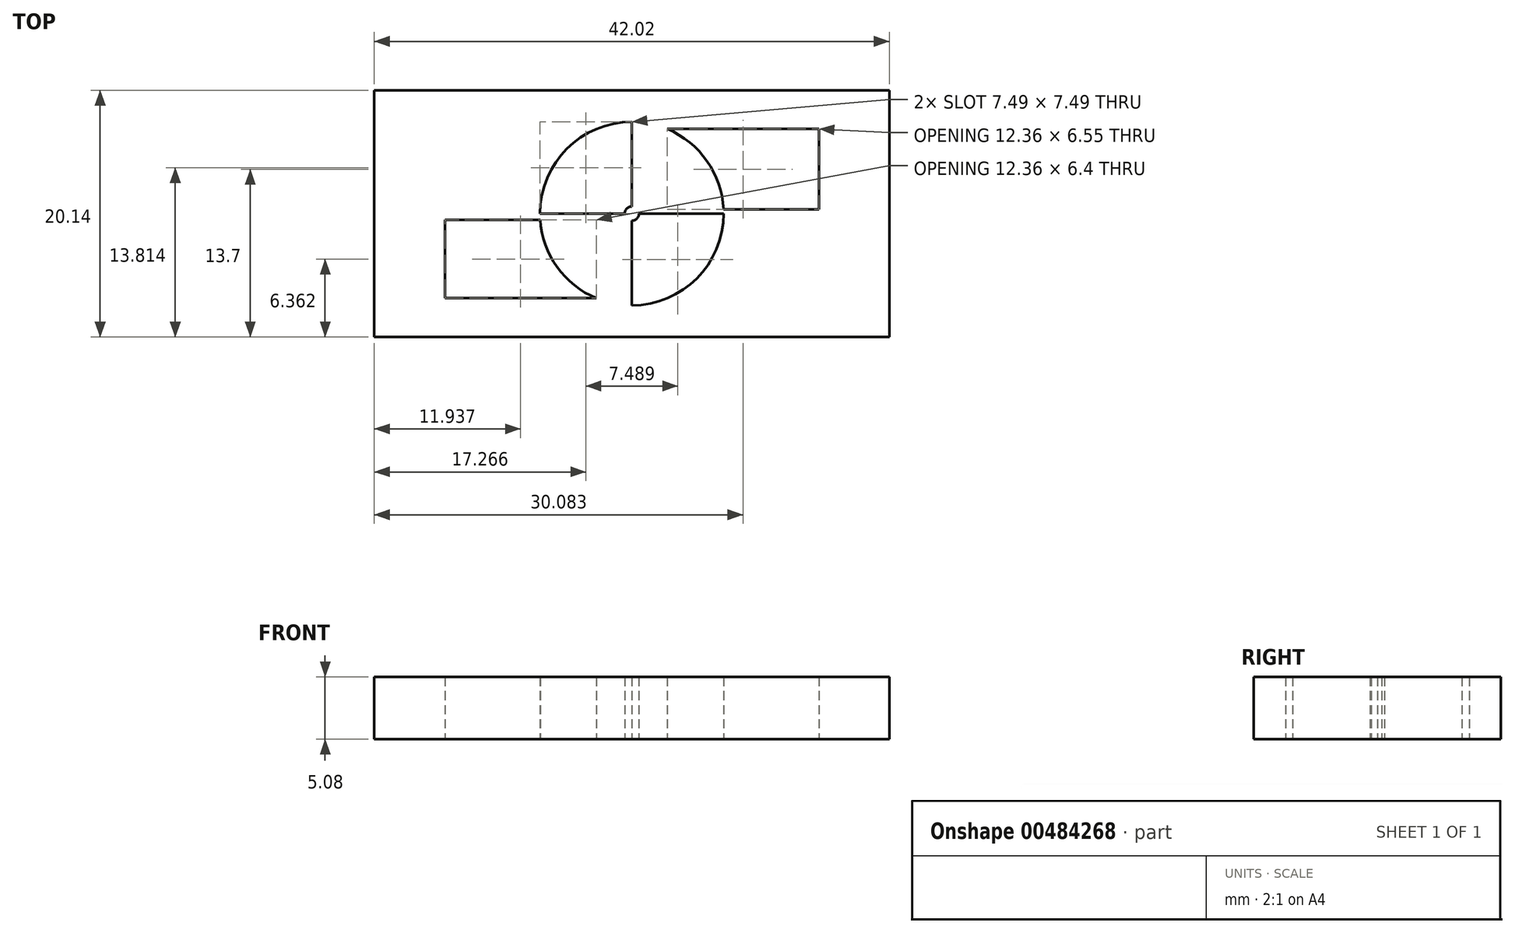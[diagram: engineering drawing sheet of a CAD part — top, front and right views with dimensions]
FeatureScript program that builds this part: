
annotation { "Feature Type Name" : "Feature", "Feature Type Description" : "" }
export const myFeature = defineFeature(function(context is Context, id is Id, definition is map)
    precondition{}
    {
        {
            var Q0;
            Q0=qCreatedBy(makeId("Top.planeOp"),FACE);
            var sketch = newSketch(context, id + "F0", { "sketchPlane" : qUnion([Q0])});
            skLineSegment(sketch, "E0.top", {"start": v(0, 10.07) * mm, "end": v(-21, 10.07) * mm});
            skLineSegment(sketch, "E0.right", {"start": v(-21, 0) * mm, "end": v(-21, 10.07) * mm});
            skLineSegment(sketch, "E1.MirrorCS", {"start": v(-21, 0) * mm, "end": v(-21, -10.07) * mm});
            skLineSegment(sketch, "E2.MirrorCS", {"start": v(0, -10.07) * mm, "end": v(-21, -10.07) * mm});
            skLineSegment(sketch, "E3.MirrorCS", {"start": v(0, 10.07) * mm, "end": v(21, 10.07) * mm});
            skLineSegment(sketch, "E4.MirrorCS", {"start": v(21, 0) * mm, "end": v(21, 10.07) * mm});
            skLineSegment(sketch, "E5.MirrorCS", {"start": v(0, -10.07) * mm, "end": v(21, -10.07) * mm});
            skLineSegment(sketch, "E6.MirrorCS", {"start": v(21, 0) * mm, "end": v(21, -10.07) * mm});
            skCircle(sketch, "E7", {"center": v(0, 0) * mm, "radius": 7.49 * mm});
            skLineSegment(sketch, "E8.right", {"start": v(-15.25, 0) * mm, "end": v(-15.25, -6.9) * mm});
            skLineSegment(sketch, "E9.MirrorCS", {"start": v(-15.25, 0) * mm, "end": v(-15.25, 6.9) * mm});
            skLineSegment(sketch, "E10.MirrorCS", {"start": v(15.25, 0) * mm, "end": v(15.25, 6.9) * mm});
            skLineSegment(sketch, "E11.MirrorCS", {"start": v(15.25, 0) * mm, "end": v(15.25, -6.9) * mm});
            skPoint(sketch, "E12", {"position": v(-2.9, 6.9) * mm});
            skPoint(sketch, "E13", {"position": v(-15.25, 6.9) * mm});
            skLineSegment(sketch, "E14", {"start": v(-15.25, 6.9) * mm, "end": v(-2.9, 6.9) * mm});
            skPoint(sketch, "E15", {"position": v(-2.9, -6.9) * mm});
            skPoint(sketch, "E16", {"position": v(2.9, -6.9) * mm});
            skPoint(sketch, "E17", {"position": v(2.9, 6.9) * mm});
            skLineSegment(sketch, "E18", {"start": v(2.9, 6.9) * mm, "end": v(15.25, 6.9) * mm});
            skLineSegment(sketch, "E19", {"start": v(2.9, -6.9) * mm, "end": v(15.25, -6.9) * mm});
            skLineSegment(sketch, "E20", {"start": v(-2.9, -6.9) * mm, "end": v(-15.25, -6.9) * mm});
            skLineSegment(sketch, "E21", {"start": v(0, 0) * mm, "end": v(0, 7.49) * mm});
            skLineSegment(sketch, "E22", {"start": v(0, 0) * mm, "end": v(0, -7.49) * mm});
            skLineSegment(sketch, "E23", {"start": v(-7.49, 0) * mm, "end": v(0, 0) * mm});
            skLineSegment(sketch, "E24", {"start": v(0, 0) * mm, "end": v(7.49, 0) * mm});
            skLineSegment(sketch, "E25", {"start": v(7.49, 0) * mm, "end": v(-7.49, 0) * mm});
            skPoint(sketch, "E26", {"position": v(-7.47, -0.5) * mm});
            skPoint(sketch, "E27", {"position": v(7.48, 0.35) * mm});
            skLineSegment(sketch, "E28", {"start": v(7.48, 0.35) * mm, "end": v(15.25, 0.35) * mm});
            skLineSegment(sketch, "E29", {"start": v(-7.47, -0.5) * mm, "end": v(-15.25, -0.5) * mm});
            skCircle(sketch, "E30", {"center": v(0, 0) * mm, "radius": 0.58 * mm});
            skSolve(sketch);
        }
        {
            var Q0;
            {var subQ1=sQuery(id+"F0.wireOp",EDGE,"E21");var subQ3=sQuery(id+"F0.wireOp",EDGE,"E30");var subQ4=makeQuery(id+"F0.imprint","INTERSECT",VERTEX,{"derivedFrom":[subQ1,subQ3]});Q0=makeQuery(id+"F0.imprint","IMPRINT",FACE,{"disambiguationData":[TD([[makeQuery(id+"F0.imprint","IMPRINT",EDGE,{"disambiguationData":[TD([[subQ4,-1.0]])],"derivedFrom":subQ3}),1.0]])]});}
            var Q1;
            {var subQ1=sQuery(id+"F0.wireOp",EDGE,"E21");var subQ3=sQuery(id+"F0.wireOp",EDGE,"E30");var subQ4=makeQuery(id+"F0.imprint","INTERSECT",VERTEX,{"derivedFrom":[subQ1,subQ3]});Q1=makeQuery(id+"F0.imprint","IMPRINT",FACE,{"disambiguationData":[TD([[makeQuery(id+"F0.imprint","IMPRINT",EDGE,{"disambiguationData":[TD([[subQ4,1.0]])],"derivedFrom":subQ3}),1.0]])]});}
            var Q2;
            {var subQ1=sQuery(id+"F0.wireOp",EDGE,"E22");var subQ3=sQuery(id+"F0.wireOp",EDGE,"E30");var subQ4=makeQuery(id+"F0.imprint","INTERSECT",VERTEX,{"derivedFrom":[subQ1,subQ3]});Q2=makeQuery(id+"F0.imprint","IMPRINT",FACE,{"disambiguationData":[TD([[makeQuery(id+"F0.imprint","IMPRINT",EDGE,{"disambiguationData":[TD([[subQ4,-1.0]])],"derivedFrom":subQ3}),1.0]])]});}
            var Q3;
            {var subQ1=sQuery(id+"F0.wireOp",EDGE,"E22");var subQ3=sQuery(id+"F0.wireOp",EDGE,"E30");var subQ4=makeQuery(id+"F0.imprint","INTERSECT",VERTEX,{"derivedFrom":[subQ1,subQ3]});Q3=makeQuery(id+"F0.imprint","IMPRINT",FACE,{"disambiguationData":[TD([[makeQuery(id+"F0.imprint","IMPRINT",EDGE,{"disambiguationData":[TD([[subQ4,1.0]])],"derivedFrom":subQ3}),1.0]])]});}
            var Q4;
            {var subQ1=sQuery(id+"F0.wireOp",EDGE,"E7");var subQ7=sQuery(id+"F0.wireOp",EDGE,"E25");var subQ8=makeQuery(id+"F0.imprint","INTERSECT",VERTEX,{"disambiguationData":[OD(1.0)],"derivedFrom":[subQ1,subQ7]});Q4=makeQuery(id+"F0.imprint","IMPRINT",FACE,{"disambiguationData":[TD([[makeQuery(id+"F0.imprint","IMPRINT",EDGE,{"disambiguationData":[TD([[subQ8,-1.0]])],"derivedFrom":subQ1}),1.0]])]});}
            var Q5;
            {var subQ0=sQuery(id+"F0.wireOp",EDGE,"E7");var subQ4=sQuery(id+"F0.wireOp",EDGE,"E25");var subQ5=makeQuery(id+"F0.imprint","INTERSECT",VERTEX,{"disambiguationData":[OD(0.0)],"derivedFrom":[subQ0,subQ4]});Q5=makeQuery(id+"F0.imprint","IMPRINT",FACE,{"disambiguationData":[TD([[makeQuery(id+"F0.imprint","IMPRINT",EDGE,{"disambiguationData":[TD([[subQ5,-1.0]])],"derivedFrom":subQ0}),1.0]])]});}
            var Q6;
            {var subQ0=sQuery(id+"F0.wireOp",EDGE,"E11.MirrorCS");Q6=makeQuery(id+"F0.imprint","IMPRINT",FACE,{"disambiguationData":[TD([[makeQuery(id+"F0.imprint","IMPRINT",EDGE,{"derivedFrom":subQ0}),-1.0]])]});}
            var Q7;
            {var subQ0=sQuery(id+"F0.wireOp",EDGE,"E9.MirrorCS");Q7=makeQuery(id+"F0.imprint","IMPRINT",FACE,{"disambiguationData":[TD([[makeQuery(id+"F0.imprint","IMPRINT",EDGE,{"derivedFrom":subQ0}),-1.0]])]});}
            var Q8;
            Q8=makeQuery(id+"F0.imprint","IMPRINT",FACE,{"disambiguationData":[TD([[makeQuery(id+"F0.imprint","IMPRINT",EDGE,{"derivedFrom":sQuery(id+"F0.wireOp",EDGE,"E0.top")}),1.0]])]});
            extrude(context, id + "F1", {"entities" : qUnion([Q0, Q1, Q2, Q3, Q4, Q5, Q6, Q7, Q8]), "depth" : 5.08 * mm});
        }
    });
